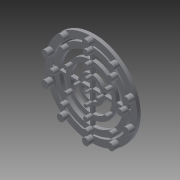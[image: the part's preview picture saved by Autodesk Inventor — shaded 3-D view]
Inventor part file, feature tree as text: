
AUTODESK INVENTOR PART (.ipt)
format: ipt  version: 2014 (Build 180170000, 170)  size: 339,968 bytes
history: native  units: in
note: dims shown in document units (in); Inventor stores cm internally (conversion verified against a paired STEP export)
features: extrude x9, sketch x2, pattern_circular x1
ambient origin geometry x8: Origin, YZ Plane, XZ Plane, XY Plane, X Axis, Y Axis, Z Axis, Center Point
bodies: Solid1 (feature_tree)
feature tree (12):
  sketch  "Sketch1"  dims[d1=0.25in d3=0.2in]
  extrude  "Extrusion1"  Depth=0.25in
  extrude  "Extrusion2"  Depth=0.1in
  extrude  "Extrusion3"  Depth=0.5in
  extrude  "Extrusion4"  Depth=0.5in
  extrude  "Extrusion5"  Depth=0.5in
  extrude  "Extrusion6"  Depth=0.25in TaperAngle=360.0deg
  extrude  "Extrusion7"  Depth=0.25in TaperAngle=360.0deg
  extrude  "Extrusion8"  Depth=0.25in TaperAngle=360.0deg
  extrude  "Extrusion9"  Depth=0.25in TaperAngle=0.0deg
  pattern_circular  "Circular Pattern1"  [2 undecoded]
  sketch  "Sketch2"  dims[d4=0.15in d5=0.1in d6=0.5in d7=0.5in d8=0.5in d9=3.1496in d11=360.0deg d13=2.3622in d15=360.0deg d17=1.5748in d19=360.0deg d21=0.25in d22=0.0in d23=3.4in d24=3.25in d25=2.2in d26=1.15in d27=0.1in d28=0.1in d29=0.1in d30=0.1in d31=0.15in d32=0.0in d33=0.15in d34=0.0in d35=0.15in d36=0.0in d37=0.15in d38=0.0in d39=0.15in d40=0.0in d41=0.15in d42=0.0in d43=4.0in d44=0.15in d45=0.0in d46=0.3in d47=0.25in d48=0.0in d49=3.937in d50=360.0deg]
note: 2 required parameter values undecoded (feature->parameter linkage not recoverable at this tier; creation-order binding heuristic only, values carry confidence <= 0.55)
